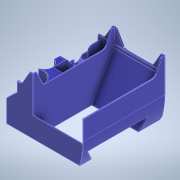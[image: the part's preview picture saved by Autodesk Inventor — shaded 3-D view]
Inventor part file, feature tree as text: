
AUTODESK INVENTOR PART (.ipt)
format: ipt  version: 2021 (Build 250183000, 183)  size: 1,035,776 bytes
history: native  units: mm
features: extrude x16, projected_geometry x13, sketch x10, fillet x5, plane x1, chamfer x1, other x1
ambient origin geometry x8: Origin, YZ Plane, XZ Plane, XY Plane, X Axis, Y Axis, Z Axis, Center Point
bodies: Solid1 (feature_tree)
feature tree (47):
  extrude  "Extrusion1"  Depth=43.0mm
  plane  "Work Plane1"
  extrude  "Extrusion2"  Depth=1.6mm
  chamfer  "Chamfer1"  Distance=0.5mm
  fillet  "Fillet1"  Radius=86.937881mm
  sketch  "Sketch4"  dims[d4=1.6mm]
  extrude  "Extrusion4"  Depth=86.937881mm
  extrude  "Extrusion5"  Depth=13.0mm
  extrude  "Extrusion6"  Depth=106.75mm
  extrude  "Extrusion7"  TaperAngle=0.0deg  [1 undecoded]
  sketch  "Sketch5"  dims[d5=1.6mm]
  extrude  "Extrusion8"  [1 undecoded]
  fillet  "Fillet2"  Radius=0.25mm
  extrude  "Extrusion9"  Depth=101.0mm
  fillet  "Fillet3"  Radius=0.25mm
  sketch  "Sketch6"  dims[d6=1.6mm]
  extrude  "Extrusion10"  Depth=0.25mm
  extrude  "Extrusion11"  Depth=12.851052mm
  extrude  "Extrusion12"  Depth=1.0mm
  extrude  "Extrusion13"  Depth=1.0mm
  extrude  "Extrusion14"  Depth=1.0mm TaperAngle=0.0deg
  sketch  "Sketch11"  dims[d11=63.0mm d14=0.5mm d15=86.937881mm d16=86.937881mm d17=13.0mm d18=106.75mm d19=0.0mm d20=-1.6mm d21=0.25mm d22=101.0mm d23=0.25mm d24=0.25mm d26=12.851052mm d27=1.0mm d28=1.0mm d29=1.0mm d30=0.0mm d33=61.0mm d34=1.0mm d35=0.25mm d36=0.5mm d38=3.0mm d39=2.0mm d40=45.0deg d41=0.5mm d42=12.0mm d43=65.0mm d44=1.2mm d45=35.0mm d46=0.0mm d47=27.0mm d48=1.6mm d49=20.0mm d50=0.5mm d51=14.0mm d52=21.0mm d53=10.0mm d54=32.5mm d55=0.8mm d56=55.2mm d57=53.2mm d58=0.0mm d59=42.0mm d60=0.0mm d61=45.2mm d62=0.0mm d63=20.0mm d64=20.0mm d65=10.0mm d66=25.0mm d67=4.0mm d68=20.0mm d69=54.2mm d70=0.0mm d71=54.2mm d72=0.0mm d73=1.0mm d74=1.0mm d75=0.75mm d76=0.5mm d77=5.0mm d78=18.0mm d79=5.0mm d80=1.6mm d81=2.0mm d82=20.038534mm d83=54.2mm d84=0.0mm d85=5.0mm d86=120.0deg d87=54.2mm d88=0.0mm d89=54.2mm d90=0.0mm d91=54.2mm d92=0.0mm d93=120.0deg d94=54.2mm d95=0.0mm d96=54.2mm d97=0.0mm d98=20.038534mm d99=54.2mm d100=0.0mm d101=54.2mm d102=0.0mm d103=5.0mm d104=5.0mm d105=1.0mm d106=0.5mm d107=5.0mm d108=0.5mm]
  extrude  "Extrusion15"  Depth=61.0mm
  extrude  "Extrusion16"  Depth=1.0mm
  fillet  "Fillet4"  Radius=3.0mm
  fillet  "Fillet5"  Radius=0.5mm
  sketch  "Sketch1"  dims[d0=30.0mm d1=43.0mm]
  sketch  "Sketch2"  dims[d2=1.0mm d3=1.6mm]
  projected_geometry  "Projected Loop1"
  projected_geometry  "Projected Loop2"
  projected_geometry  "Projected Loop4"
  projected_geometry  "Projected Loop5"
  projected_geometry  "Projected Loop6"
  projected_geometry  "Projected Loop7"
  projected_geometry  "Projected Loop8"
  projected_geometry  "Projected Loop9"
  sketch  "Sketch7"  dims[d7=108.4mm]
  projected_geometry  "Projected Loop10"
  other  "Srf1"
  sketch  "Sketch8"  dims[d8=51.0mm]
  projected_geometry  "Projected Loop11"
  sketch  "Sketch9"  dims[d9=31.5mm]
  projected_geometry  "Projected Loop12"
  sketch  "Sketch10"  dims[d10=18.2mm]
  projected_geometry  "Projected Loop13"
  projected_geometry  "Projected Loop14"
  extrude  "ExtrusionSrf1"  Depth=12.0mm
note: 2 required parameter values undecoded (feature->parameter linkage not recoverable at this tier; creation-order binding heuristic only, values carry confidence <= 0.55)
